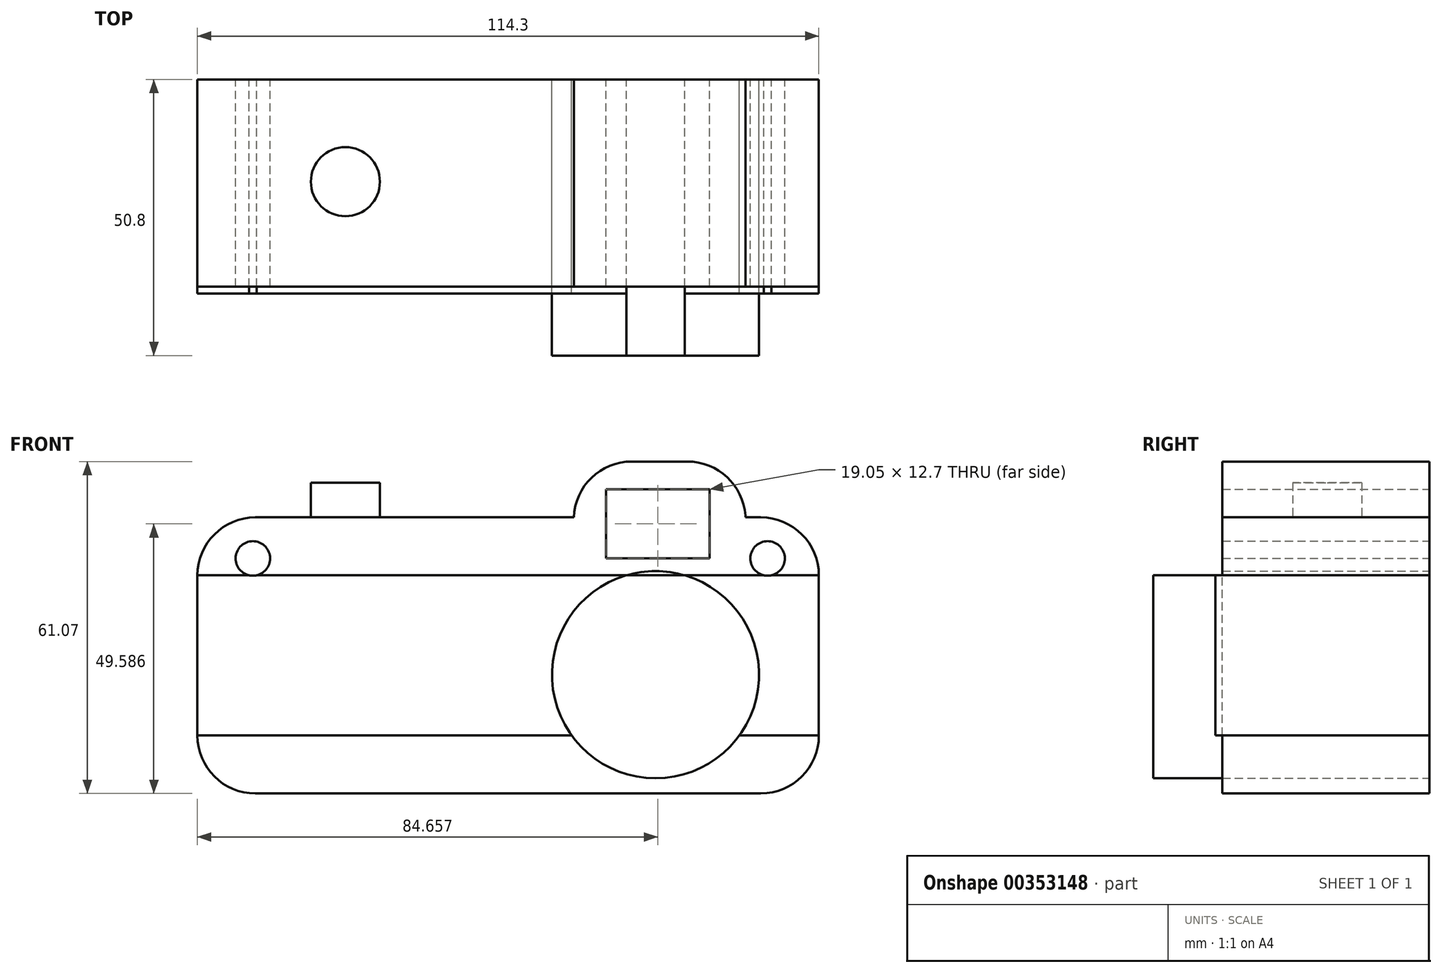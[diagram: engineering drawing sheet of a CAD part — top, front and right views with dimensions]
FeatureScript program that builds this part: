
annotation { "Feature Type Name" : "Feature", "Feature Type Description" : "" }
export const myFeature = defineFeature(function(context is Context, id is Id, definition is map)
    precondition{}
    {
        {
            var Q0;
            Q0=qCreatedBy(makeId("Front.planeOp"),FACE);
            var sketch = newSketch(context, id + "F0", { "sketchPlane" : qUnion([Q0])});
            skLineSegment(sketch, "E0.bottom", {"start": v(-44.22, 28.95) * mm, "end": v(48.75, 28.95) * mm});
            skLineSegment(sketch, "E0.top", {"start": v(-44.22, -21.85) * mm, "end": v(48.75, -21.85) * mm});
            skLineSegment(sketch, "E0.left", {"start": v(-54.88, 18.28) * mm, "end": v(-54.88, -11.18) * mm});
            skLineSegment(sketch, "E0.right", {"start": v(59.42, 18.28) * mm, "end": v(59.42, -11.18) * mm});
            skLineSegment(sketch, "E1", {"start": v(14.37, 27.77) * mm, "end": v(14.28, 28.95) * mm});
            skLineSegment(sketch, "E2", {"start": v(25, 39.22) * mm, "end": v(35.26, 39.22) * mm});
            skLineSegment(sketch, "E3", {"start": v(45.9, 29.28) * mm, "end": v(45.92, 28.95) * mm});
            skLineSegment(sketch, "E4.bottom", {"start": v(20.25, 34.09) * mm, "end": v(39.3, 34.09) * mm});
            skLineSegment(sketch, "E4.top", {"start": v(20.25, 21.39) * mm, "end": v(39.3, 21.39) * mm});
            skLineSegment(sketch, "E4.left", {"start": v(20.25, 34.09) * mm, "end": v(20.25, 21.39) * mm});
            skLineSegment(sketch, "E4.right", {"start": v(39.3, 34.09) * mm, "end": v(39.3, 21.39) * mm});
            skPoint(sketch, "E5", {"position": v(13.9, 34.09) * mm});
            skCircle(sketch, "E6", {"center": v(29.38, 0) * mm, "radius": 19.05 * mm});
            skCircle(sketch, "E7", {"center": v(-44.69, 21.39) * mm, "radius": 3.18 * mm});
            skCircle(sketch, "E8", {"center": v(50, 21.39) * mm, "radius": 3.18 * mm});
            skPoint(sketch, "E9.visualSharp", {"position": v(-54.88, 28.95) * mm});
            skArc(sketch, "E9.filletArc", {"start": v(-44.22, 28.95) * mm, "mid": v(-51.76, 25.83) * mm, "end": v(-54.88, 18.28) * mm});
            skPoint(sketch, "E10.visualSharp", {"position": v(-54.88, -21.85) * mm});
            skArc(sketch, "E10.filletArc", {"start": v(-54.88, -11.18) * mm, "mid": v(-51.76, -18.72) * mm, "end": v(-44.22, -21.85) * mm});
            skPoint(sketch, "E11.visualSharp", {"position": v(59.42, -21.85) * mm});
            skArc(sketch, "E11.filletArc", {"start": v(48.75, -21.85) * mm, "mid": v(56.3, -18.72) * mm, "end": v(59.42, -11.18) * mm});
            skPoint(sketch, "E12.visualSharp", {"position": v(59.42, 28.95) * mm});
            skArc(sketch, "E12.filletArc", {"start": v(59.42, 18.28) * mm, "mid": v(56.3, 25.83) * mm, "end": v(48.75, 28.95) * mm});
            skPoint(sketch, "E13.visualSharp", {"position": v(13.53, 39.22) * mm});
            skArc(sketch, "E13.filletArc", {"start": v(25, 39.22) * mm, "mid": v(17.2, 35.81) * mm, "end": v(14.37, 27.77) * mm});
            skPoint(sketch, "E14.visualSharp", {"position": v(45.22, 39.22) * mm});
            skArc(sketch, "E14.filletArc", {"start": v(45.9, 29.28) * mm, "mid": v(42.54, 36.35) * mm, "end": v(35.26, 39.22) * mm});
            skLineSegment(sketch, "E15.bottom", {"start": v(0, 25.81) * mm, "end": v(7.7, 25.81) * mm});
            skLineSegment(sketch, "E15.top", {"start": v(0, 22.1) * mm, "end": v(7.7, 22.1) * mm});
            skLineSegment(sketch, "E15.left", {"start": v(0, 25.81) * mm, "end": v(0, 22.1) * mm});
            skLineSegment(sketch, "E15.right", {"start": v(7.7, 25.81) * mm, "end": v(7.7, 22.1) * mm});
            skLineSegment(sketch, "E16", {"start": v(-54.88, 18.28) * mm, "end": v(24.03, 18.28) * mm});
            skLineSegment(sketch, "E17", {"start": v(-54.88, -11.18) * mm, "end": v(13.96, -11.18) * mm});
            skLineSegment(sketch, "E18", {"start": v(44.8, -11.18) * mm, "end": v(59.42, -11.18) * mm});
            skLineSegment(sketch, "E19", {"start": v(24.03, 18.28) * mm, "end": v(59.42, 18.28) * mm});
            skSolve(sketch);
        }
        {
            var Q0;
            {var subQ0=sQuery(id+"F0.wireOp",EDGE,"E1");Q0=makeQuery(id+"F0.imprint","IMPRINT",FACE,{"disambiguationData":[TD([[makeQuery(id+"F0.imprint","IMPRINT",EDGE,{"derivedFrom":subQ0}),-1.0]])]});}
            var Q1;
            {var subQ0=sQuery(id+"F0.wireOp",EDGE,"E1");Q1=makeQuery(id+"F0.imprint","IMPRINT",FACE,{"disambiguationData":[TD([[makeQuery(id+"F0.imprint","IMPRINT",EDGE,{"derivedFrom":subQ0}),-1.0]])]});}
            var Q2;
            Q2=makeQuery(id+"F0.imprint","IMPRINT",FACE,{"disambiguationData":[TD([[makeQuery(id+"F0.imprint","IMPRINT",EDGE,{"derivedFrom":sQuery(id+"F0.wireOp",EDGE,"E0.top")}),1.0]])]});
            var Q3;
            {var subQ14=sQuery(id+"F0.wireOp",EDGE,"E4.top");Q3=makeQuery(id+"F0.imprint","IMPRINT",FACE,{"disambiguationData":[TD([[makeQuery(id+"F0.imprint","IMPRINT",EDGE,{"derivedFrom":subQ14}),-1.0]])]});}
            var Q4;
            {var subQ1=sQuery(id+"F0.wireOp",EDGE,"E6");var subQ3=makeQuery(id+"F0.imprint","INTERSECT",VERTEX,{"derivedFrom":[subQ1,sQuery(id+"F0.wireOp",EDGE,"E17")]});Q4=makeQuery(id+"F0.imprint","IMPRINT",FACE,{"disambiguationData":[TD([[makeQuery(id+"F0.imprint","IMPRINT",EDGE,{"disambiguationData":[TD([[subQ3,-1.0]])],"derivedFrom":subQ1}),1.0]])]});}
            var Q5;
            {var subQ0=sQuery(id+"F0.wireOp",EDGE,"E15.bottom");Q5=makeQuery(id+"F0.imprint","IMPRINT",FACE,{"disambiguationData":[TD([[makeQuery(id+"F0.imprint","IMPRINT",EDGE,{"derivedFrom":subQ0}),-1.0]])]});}
            extrude(context, id + "F1", {"entities" : qUnion([Q0, Q1, Q2, Q3, Q4, Q5]), "depth" : 38.1 * mm});
        }
        {
            var Q0;
            Q0=makeQuery(id+"F0.imprint","IMPRINT",FACE,{"disambiguationData":[TD([[makeQuery(id+"F0.imprint","IMPRINT",EDGE,{"derivedFrom":sQuery(id+"F0.wireOp",EDGE,"E6")}),1.0]])]});
            extrude(context, id + "F2", {"entities" : qUnion([Q0]), "depth" : 50.8 * mm});
        }
        {
            var Q0;
            {var subQ0=sQuery(id+"F0.wireOp",EDGE,"E0.bottom");Q0=makeQuery(id+"F1.opExtrude","SWEPT_FACE",FACE,{"disambiguationData":[OSD([subQ0]),TDD([makeQuery(id+"F0.imprint","IMPRINT",EDGE,{"disambiguationData":[TD([[makeQuery(id+"F0.imprint","INTERSECT",VERTEX,{"derivedFrom":[subQ0,sQuery(id+"F0.wireOp",EDGE,"E0.left")]}),-1.0]])],"derivedFrom":subQ0})])]});}
            var sketch = newSketch(context, id + "F3", { "sketchPlane" : qUnion([Q0])});
            skCircle(sketch, "E20", {"center": v(-27.67, -18.82) * mm, "radius": 6.35 * mm});
            skSolve(sketch);
        }
        {
            var Q0;
            Q0=makeQuery(id+"F3.imprint","IMPRINT",FACE,{"disambiguationData":[TD([[makeQuery(id+"F3.imprint","IMPRINT",EDGE,{"derivedFrom":sQuery(id+"F3.wireOp",EDGE,"E20")}),1.0]])]});
            extrude(context, id + "F4", {"entities" : qUnion([Q0]), "depth" : 6.35 * mm});
        }
        {
            var Q0;
            Q0=makeQuery(id+"F0.imprint","IMPRINT",FACE,{"disambiguationData":[TD([[makeQuery(id+"F0.imprint","IMPRINT",EDGE,{"derivedFrom":sQuery(id+"F0.wireOp",EDGE,"E15.bottom")}),-1.0]])]});
            extrude(context, id + "F5", {"entities" : qUnion([Q0]), "operationType" : NewBodyOperationType.ADD, "depth" : 34.3 * mm});
        }
        {
            var Q0;
            {var subQ8=sQuery(id+"F0.wireOp",EDGE,"E0.left");Q0=makeQuery(id+"F0.imprint","IMPRINT",FACE,{"disambiguationData":[TD([[makeQuery(id+"F0.imprint","IMPRINT",EDGE,{"derivedFrom":subQ8}),1.0]])]});}
            var Q1;
            {var subQ7=sQuery(id+"F0.wireOp",EDGE,"E0.right");Q1=makeQuery(id+"F0.imprint","IMPRINT",FACE,{"disambiguationData":[TD([[makeQuery(id+"F0.imprint","IMPRINT",EDGE,{"derivedFrom":subQ7}),-1.0]])]});}
            extrude(context, id + "F6", {"entities" : qUnion([Q0, Q1]), "depth" : 39.37 * mm});
        }
        {
            var Q0;
            {var subQ0=sQuery(id+"F0.wireOp",EDGE,"E15.bottom");Q0=makeQuery(id+"F0.imprint","IMPRINT",FACE,{"disambiguationData":[TD([[makeQuery(id+"F0.imprint","IMPRINT",EDGE,{"derivedFrom":subQ0}),-1.0]])]});}
            extrude(context, id + "F7", {"entities" : qUnion([Q0]), "operationType" : NewBodyOperationType.ADD, "depth" : 34.3 * mm});
        }
        {
            var Q0;
            {var subQ0=sQuery(id+"F0.wireOp",EDGE,"E15.bottom");Q0=makeQuery(id+"F0.imprint","IMPRINT",FACE,{"disambiguationData":[TD([[makeQuery(id+"F0.imprint","IMPRINT",EDGE,{"derivedFrom":subQ0}),-1.0]])]});}
            extrude(context, id + "F8", {"entities" : qUnion([Q0]), "operationType" : NewBodyOperationType.ADD, "depth" : 38.1 * mm});
        }
        {
            var Q0;
            {var subQ1=sQuery(id+"F0.wireOp",EDGE,"E2");Q0=makeQuery(id+"F0.imprint","IMPRINT",FACE,{"disambiguationData":[TD([[makeQuery(id+"F0.imprint","IMPRINT",EDGE,{"derivedFrom":subQ1}),-1.0]])]});}
            extrude(context, id + "F9", {"entities" : qUnion([Q0]), "operationType" : NewBodyOperationType.ADD, "depth" : 38.1 * mm});
        }
    });
